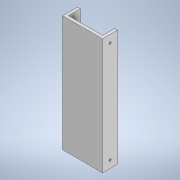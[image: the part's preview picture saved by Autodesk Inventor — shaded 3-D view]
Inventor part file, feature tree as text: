
AUTODESK INVENTOR PART (.ipt)
format: ipt  version: 2020 (Build 240168000, 168)  size: 137,728 bytes
history: native  units: mm
features: sketch x3, extrude x2, other x1, hole x1, mirror x1
ambient origin geometry x8: Origin, YZ Plane, XZ Plane, XY Plane, X Axis, Y Axis, Z Axis, Center Point
bodies: Body1 (feature_tree)
feature tree (8):
  other  "Твердое тело1"
  extrude  "Выдавливание1"  Depth=27.0mm
  sketch  "Эскиз2"
  extrude  "Выдавливание3"  Depth=10.0mm
  hole  "Отверстие1"  [1 undecoded]
  mirror  "Зеркальное отражение1"
  sketch  "Эскиз1"
  sketch  "Эскиз3"
note: 1 required parameter value undecoded (feature->parameter linkage not recoverable at this tier; creation-order binding heuristic only, values carry confidence <= 0.55)
